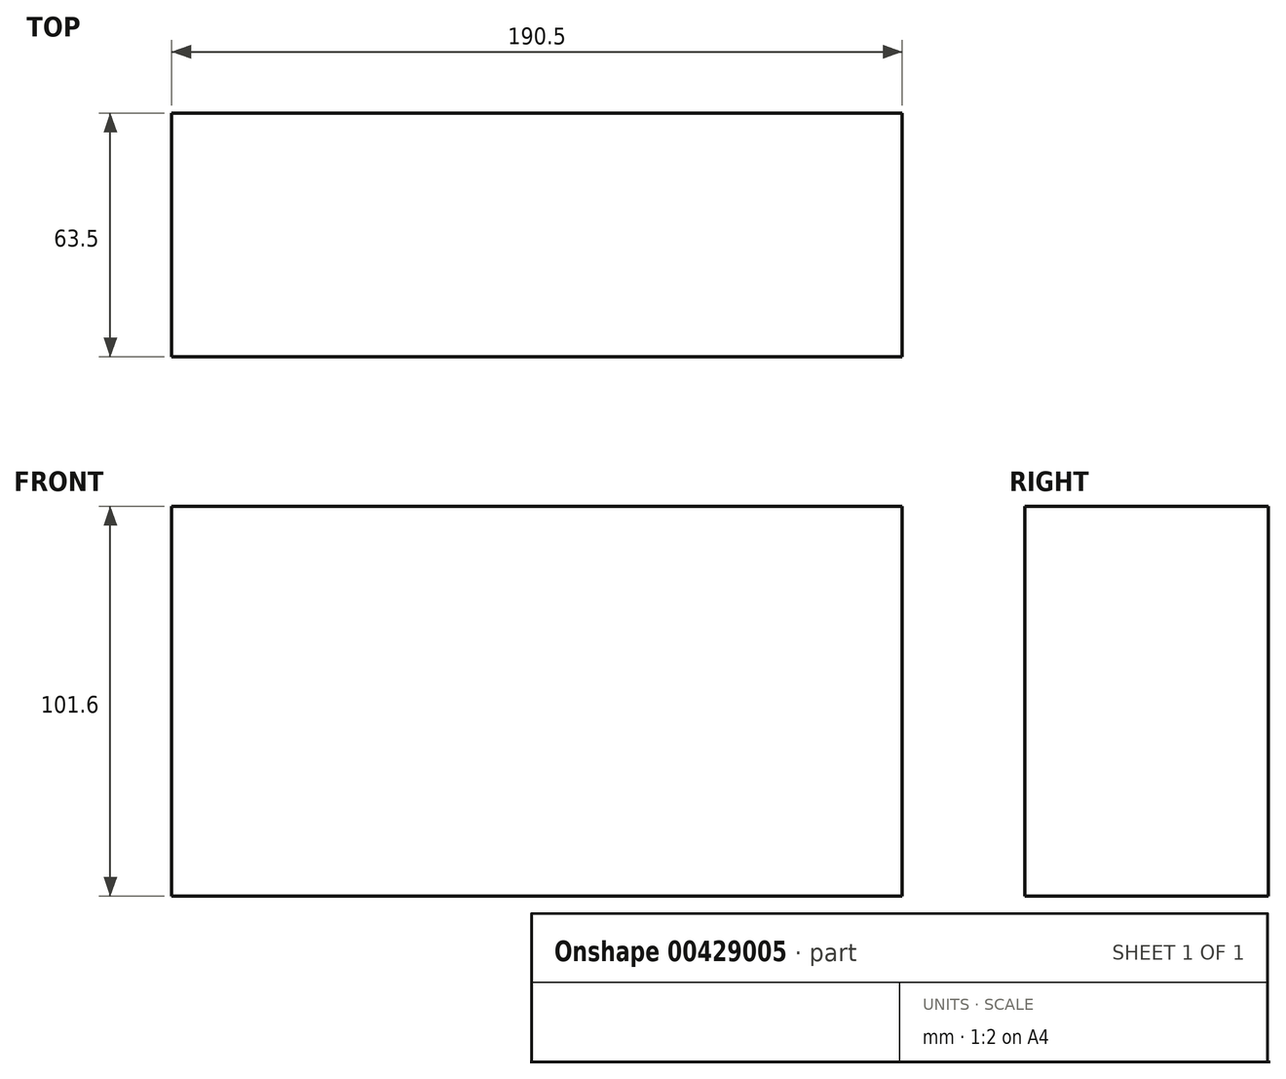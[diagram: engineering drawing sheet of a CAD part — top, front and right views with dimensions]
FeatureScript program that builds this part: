
annotation { "Feature Type Name" : "Feature", "Feature Type Description" : "" }
export const myFeature = defineFeature(function(context is Context, id is Id, definition is map)
    precondition{}
    {
        {
            var Q0;
            Q0=qCreatedBy(makeId("Front.planeOp"),FACE);
            var sketch = newSketch(context, id + "F0", { "sketchPlane" : qUnion([Q0])});
            skLineSegment(sketch, "E0.bottom", {"start": v(-95.25, 50.8) * mm, "end": v(95.25, 50.8) * mm});
            skLineSegment(sketch, "E0.top", {"start": v(-95.25, -50.8) * mm, "end": v(95.25, -50.8) * mm});
            skLineSegment(sketch, "E0.left", {"start": v(-95.25, 50.8) * mm, "end": v(-95.25, -50.8) * mm});
            skLineSegment(sketch, "E0.right", {"start": v(95.25, 50.8) * mm, "end": v(95.25, -50.8) * mm});
            skPoint(sketch, "E0.middle", {"position": v(0, 0) * mm});
            skSolve(sketch);
        }
        {
            var Q0;
            Q0=makeQuery(id+"F0.imprint","IMPRINT",FACE,{"disambiguationData":[TD([[makeQuery(id+"F0.imprint","IMPRINT",EDGE,{"derivedFrom":sQuery(id+"F0.wireOp",EDGE,"E0.bottom")}),-1.0]])]});
            extrude(context, id + "F1", {"entities" : qUnion([Q0]), "depth" : 63.5 * mm});
        }
    });
